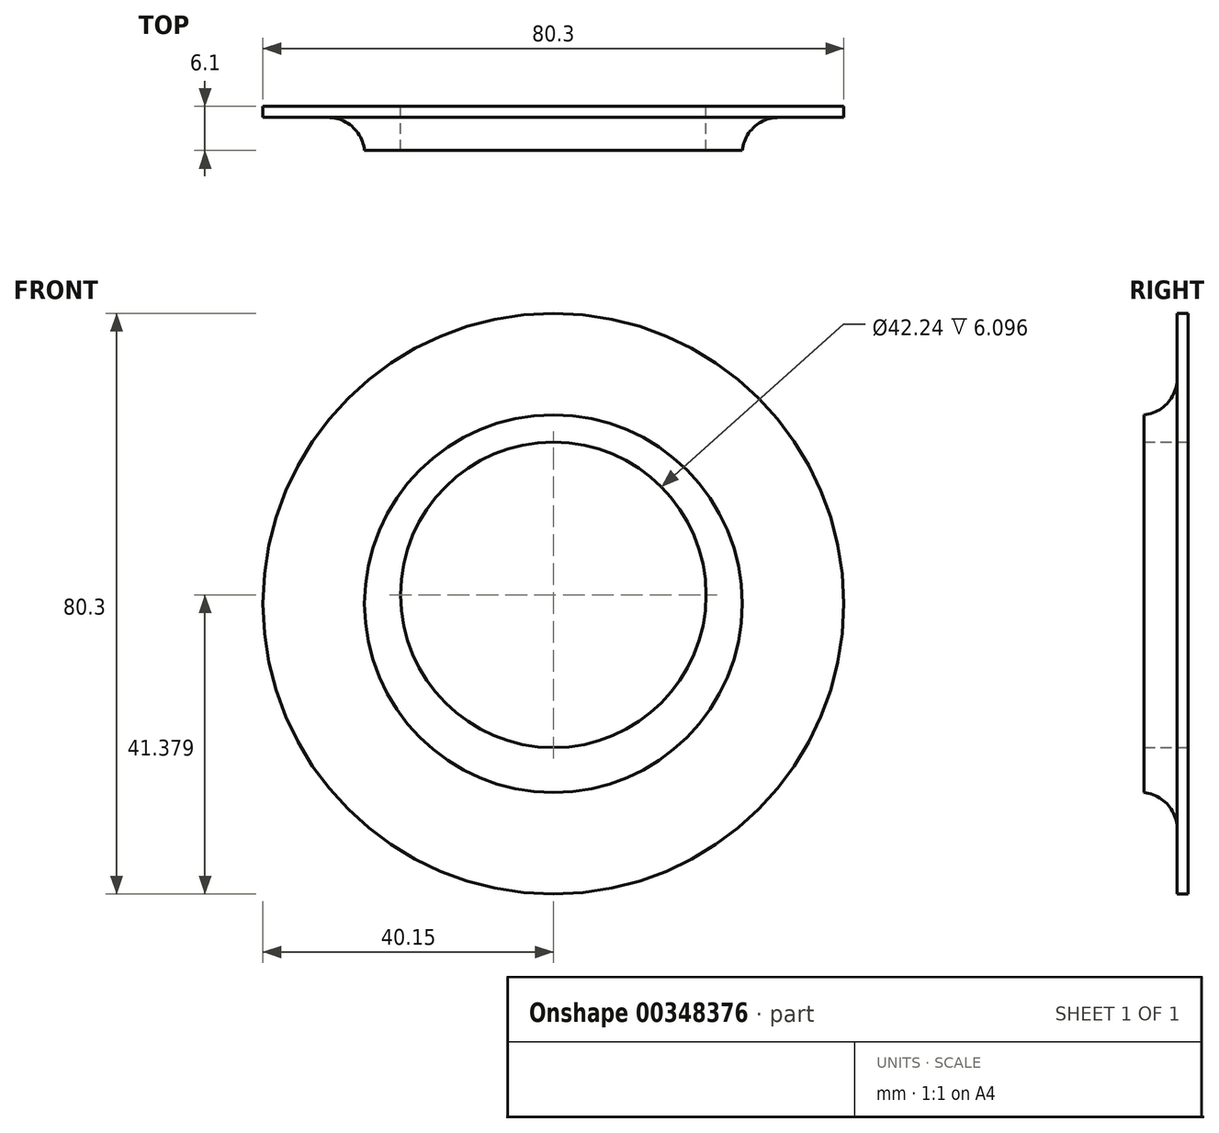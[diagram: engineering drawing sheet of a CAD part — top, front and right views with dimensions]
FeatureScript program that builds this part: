
annotation { "Feature Type Name" : "Feature", "Feature Type Description" : "" }
export const myFeature = defineFeature(function(context is Context, id is Id, definition is map)
    precondition{}
    {
        {
            var Q0;
            Q0=qCreatedBy(makeId("Front.planeOp"),FACE);
            var sketch = newSketch(context, id + "F0", { "sketchPlane" : qUnion([Q0])});
            skCircle(sketch, "E0", {"center": v(0, 1.23) * mm, "radius": 21.12 * mm});
            skLineSegment(sketch, "E1", {"start": v(0, 22.35) * mm, "end": v(0, 26.11) * mm});
            skCircle(sketch, "E2", {"center": v(0, 0) * mm, "radius": 26.12 * mm});
            skCircle(sketch, "E3", {"center": v(0, 0) * mm, "radius": 40.15 * mm});
            skSolve(sketch);
        }
        {
            var Q0;
            Q0=makeQuery(id+"F0.imprint","IMPRINT",FACE,{"disambiguationData":[TD([[makeQuery(id+"F0.imprint","IMPRINT",EDGE,{"derivedFrom":sQuery(id+"F0.wireOp",EDGE,"E2")}),-1.0]])]});
            var Q1;
            Q1=makeQuery(id+"F0.imprint","IMPRINT",FACE,{"disambiguationData":[TD([[makeQuery(id+"F0.imprint","IMPRINT",EDGE,{"derivedFrom":sQuery(id+"F0.wireOp",EDGE,"E0")}),-1.0]])]});
            extrude(context, id + "F1", {"entities" : qUnion([Q0, Q1]), "depth" : 1.52 * mm});
        }
        {
            var Q0;
            Q0=makeQuery(id+"F0.imprint","IMPRINT",FACE,{"disambiguationData":[TD([[makeQuery(id+"F0.imprint","IMPRINT",EDGE,{"derivedFrom":sQuery(id+"F0.wireOp",EDGE,"E0")}),-1.0]])]});
            extrude(context, id + "F2", {"entities" : qUnion([Q0]), "operationType" : NewBodyOperationType.ADD, "depth" : 6.1 * mm});
        }
        {
            var Q0;
            Q0=makeQuery(id+"F2.boolean.opBoolean","INTERSECT",EDGE,{"derivedFrom":[makeQuery(id+"F1.opExtrude","CAP_FACE",FACE,{"disambiguationData":[OSD([sQuery(id+"F0.wireOp",EDGE,"E0"),sQuery(id+"F0.wireOp",EDGE,"E3")])],"isStart":false}),makeQuery(id+"F2.opExtrude","SWEPT_FACE",FACE,{"disambiguationData":[OSD([sQuery(id+"F0.wireOp",EDGE,"E2")])]})]});
            fillet(context, id + "F3", {"entities" : qUnion([Q0]), "radius" : 5.08 * mm, "tangentPropagation" : true, "allowEdgeOverflow" : false});
        }
    });
